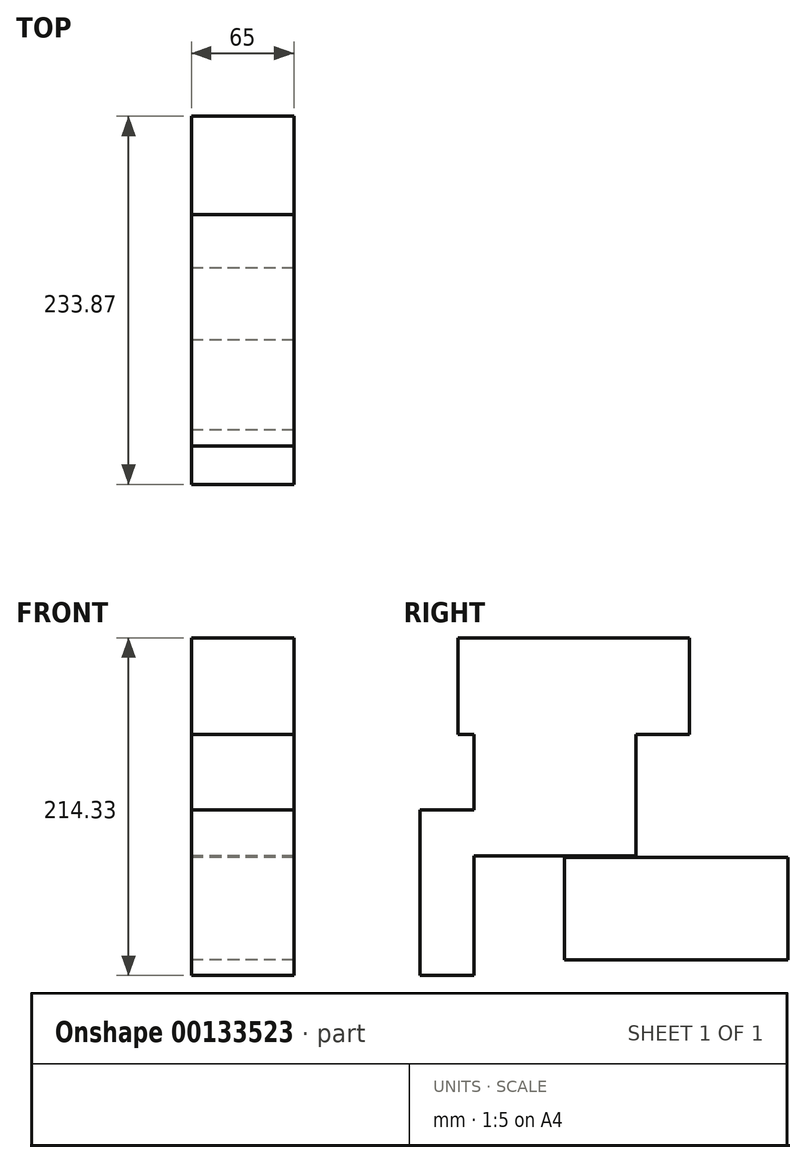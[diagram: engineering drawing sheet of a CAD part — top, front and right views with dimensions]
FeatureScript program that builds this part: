
annotation { "Feature Type Name" : "Feature", "Feature Type Description" : "" }
export const myFeature = defineFeature(function(context is Context, id is Id, definition is map)
    precondition{}
    {
        {
            var Q0;
            Q0=qCreatedBy(makeId("Right.planeOp"),FACE);
            var sketch = newSketch(context, id + "F0", { "sketchPlane" : qUnion([Q0])});
            skLineSegment(sketch, "E0.bottom", {"start": v(45.46, -29.2) * mm, "end": v(-57.33, -29.2) * mm});
            skLineSegment(sketch, "E0.top", {"start": v(45.46, 48.12) * mm, "end": v(-57.33, 48.12) * mm});
            skLineSegment(sketch, "E0.left", {"start": v(45.46, -29.2) * mm, "end": v(45.46, 48.12) * mm});
            skLineSegment(sketch, "E0.right", {"start": v(-57.33, -29.2) * mm, "end": v(-57.33, 48.12) * mm});
            skLineSegment(sketch, "E1.bottom", {"start": v(79.5, 48.12) * mm, "end": v(-67.6, 48.12) * mm});
            skLineSegment(sketch, "E1.top", {"start": v(79.5, 109.4) * mm, "end": v(-67.6, 109.4) * mm});
            skLineSegment(sketch, "E1.left", {"start": v(79.5, 48.12) * mm, "end": v(79.5, 109.4) * mm});
            skLineSegment(sketch, "E1.right", {"start": v(-67.6, 48.12) * mm, "end": v(-67.6, 109.4) * mm});
            skLineSegment(sketch, "E2.bottom", {"start": v(-91.84, 0) * mm, "end": v(-57.33, 0) * mm});
            skLineSegment(sketch, "E2.top", {"start": v(-91.84, -104.93) * mm, "end": v(-57.33, -104.93) * mm});
            skLineSegment(sketch, "E2.left", {"start": v(-91.84, 0) * mm, "end": v(-91.84, -104.93) * mm});
            skLineSegment(sketch, "E2.right", {"start": v(-57.33, 0) * mm, "end": v(-57.33, -104.93) * mm});
            skLineSegment(sketch, "E3.bottom", {"start": v(0, -95.11) * mm, "end": v(142.03, -95.11) * mm});
            skLineSegment(sketch, "E3.top", {"start": v(0, -29.92) * mm, "end": v(142.03, -29.92) * mm});
            skLineSegment(sketch, "E3.left", {"start": v(0, -95.11) * mm, "end": v(0, -29.92) * mm});
            skLineSegment(sketch, "E3.right", {"start": v(142.03, -95.11) * mm, "end": v(142.03, -29.92) * mm});
            skSolve(sketch);
        }
        {
            var Q0;
            Q0=makeQuery(id+"F0.imprint","IMPRINT",FACE,{"disambiguationData":[TD([[makeQuery(id+"F0.imprint","IMPRINT",EDGE,{"derivedFrom":sQuery(id+"F0.wireOp",EDGE,"E1.top")}),1.0]])]});
            var Q1;
            Q1=makeQuery(id+"F0.imprint","IMPRINT",FACE,{"disambiguationData":[TD([[makeQuery(id+"F0.imprint","IMPRINT",EDGE,{"derivedFrom":sQuery(id+"F0.wireOp",EDGE,"E3.bottom")}),1.0]])]});
            var Q2;
            {var subQ3=sQuery(id+"F0.wireOp",EDGE,"E0.bottom");Q2=makeQuery(id+"F0.imprint","IMPRINT",FACE,{"disambiguationData":[TD([[makeQuery(id+"F0.imprint","IMPRINT",EDGE,{"derivedFrom":subQ3}),-1.0]])]});}
            var Q3;
            {var subQ2=sQuery(id+"F0.wireOp",EDGE,"E2.bottom");Q3=makeQuery(id+"F0.imprint","IMPRINT",FACE,{"disambiguationData":[TD([[makeQuery(id+"F0.imprint","IMPRINT",EDGE,{"derivedFrom":subQ2}),-1.0]])]});}
            extrude(context, id + "F1", {"entities" : qUnion([Q0, Q1, Q2, Q3]), "endBound" : BoundingType.SYMMETRIC, "depth" : 65 * mm});
        }
    });
